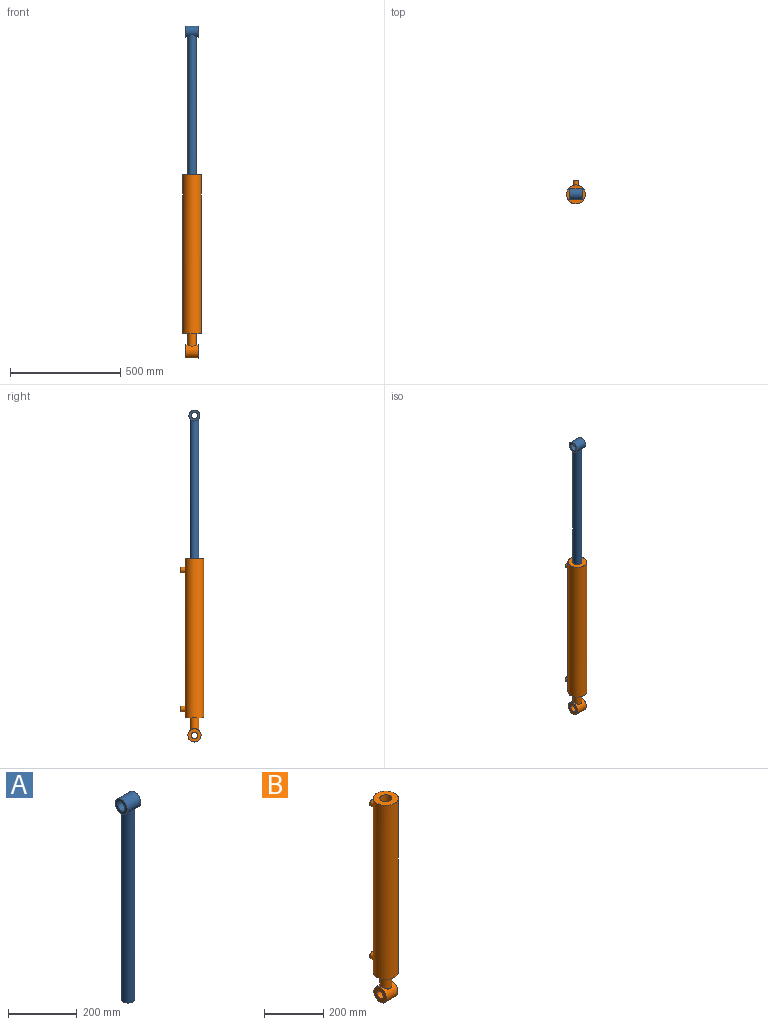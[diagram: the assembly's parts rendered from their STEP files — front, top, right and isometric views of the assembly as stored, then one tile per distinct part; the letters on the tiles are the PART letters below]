
ASSEMBLY  parts=2 mates=1
PART A: 6 faces, bbox 55x50x725 mm
  f0: cylinder r=20mm len=685mm, axis (0,0,-1), area 85411.9mm2, adj f1,f2
  f1: plane 40x40mm, normal (0,0,-1), area 1256.6mm2, adj f0
  f2: cylinder r=25mm len=55mm, axis (-1,0,0), area 7244.3mm2, adj f0,f3,f4
  f3: plane 50x50mm, normal (1,0,0), area 1244.8mm2, adj f2,f5
  f4: plane 50x50mm, normal (-1,0,0), area 1244.8mm2, adj f2,f5
  f5: cylinder r=15.12mm len=55mm, axis (1,0,0), area 5226.8mm2, adj f3,f4
PART B: 14 faces, bbox 85x107.5x830 mm
  f0: cylinder r=20mm len=57.64mm, axis (0,0,-1), area 6744.7mm2, adj f3,f10
  f1: cylinder r=42.5mm len=720mm, axis (0,0,-1), area 191273.2mm2, adj f2,f3,f4,f6
  f2: plane 85x85mm, normal (0,0,1), area 4417.9mm2, adj f1,f12
  f3: plane 85x85mm, normal (0,0,-1), area 4417.9mm2, adj f0,f1
  f4: cylinder r=12.5mm len=25mm, axis (0,-1,0), area 1840.5mm2, adj f1,f5
  f5: plane 25x25mm, normal (0,1,0), area 490.9mm2, adj f4
  f6: cylinder r=12.5mm len=25mm, axis (0,-1,0), area 1840.5mm2, adj f1,f7
  f7: plane 25x25mm, normal (0,1,0), area 490.9mm2, adj f6
  f8: plane 60x60mm, normal (1,0,0), area 2120.6mm2, adj f10,f11
  f9: plane 60x60mm, normal (-1,0,0), area 2120.6mm2, adj f10,f11
  f10: cylinder r=30mm len=60mm, axis (-1,0,0), area 9027.5mm2, adj f0,f8,f9
  f11: cylinder r=15mm len=55mm, axis (-1,0,0), area 5183.6mm2, adj f8,f9
  f12: cylinder r=20mm len=50mm, axis (0,0,1), area 6283.2mm2, adj f2,f13
  f13: plane 40x40mm, normal (0,0,1), area 1256.6mm2, adj f12
PLACE A rot(axis=(0.9,0.36,-0.24),0deg) t=(420.95,628.91,1278.87)mm
PLACE B rot(axis=(0.9,0.36,-0.24),0deg) t=(420.95,628.91,528.87)mm
MATE slider A.f0 <-> B.f0  axis (0,0,-1) through (420.95,628.91,1278.87)mm
